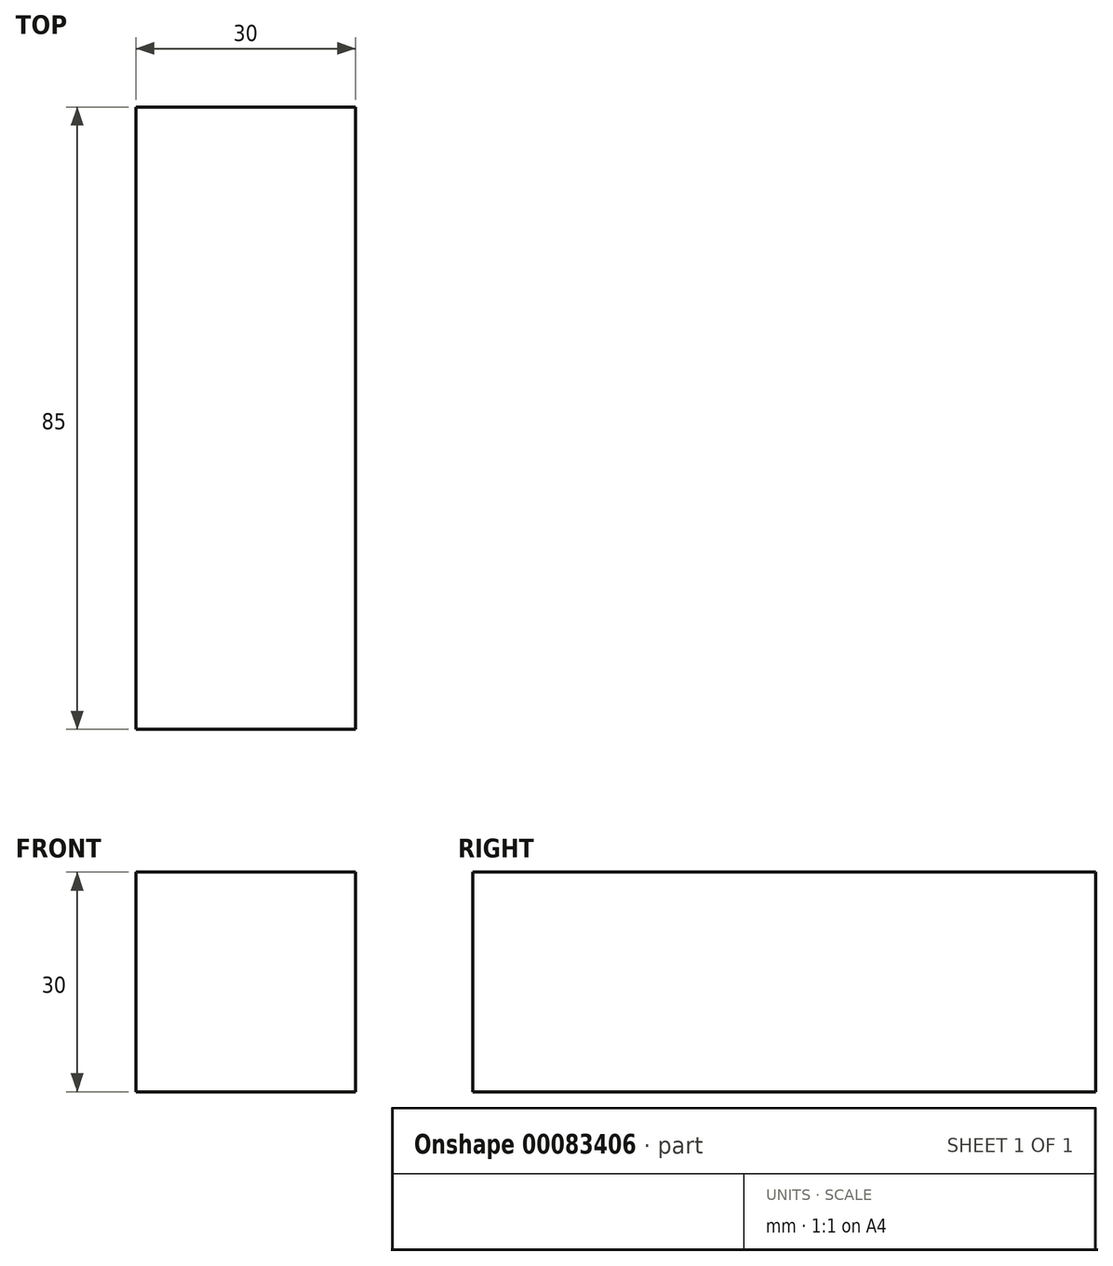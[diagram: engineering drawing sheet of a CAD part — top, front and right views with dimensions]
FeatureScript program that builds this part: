
annotation { "Feature Type Name" : "Feature", "Feature Type Description" : "" }
export const myFeature = defineFeature(function(context is Context, id is Id, definition is map)
    precondition{}
    {
        {
            var Q0;
            Q0=qCreatedBy(makeId("Right.planeOp"),FACE);
            var sketch = newSketch(context, id + "F0", { "sketchPlane" : qUnion([Q0])});
            skLineSegment(sketch, "E0.bottom", {"start": v(42.5, 15) * mm, "end": v(-42.5, 15) * mm});
            skLineSegment(sketch, "E0.top", {"start": v(42.5, -15) * mm, "end": v(-42.5, -15) * mm});
            skLineSegment(sketch, "E0.left", {"start": v(42.5, 15) * mm, "end": v(42.5, -15) * mm});
            skLineSegment(sketch, "E0.right", {"start": v(-42.5, 15) * mm, "end": v(-42.5, -15) * mm});
            skPoint(sketch, "E0.middle", {"position": v(0, 0) * mm});
            skLineSegment(sketch, "E1.bottom", {"start": v(88.8, 61.92) * mm, "end": v(68.8, 61.92) * mm});
            skLineSegment(sketch, "E1.top", {"start": v(88.8, 31.92) * mm, "end": v(68.8, 31.92) * mm});
            skLineSegment(sketch, "E1.left", {"start": v(88.8, 61.92) * mm, "end": v(88.8, 31.92) * mm});
            skLineSegment(sketch, "E1.right", {"start": v(68.8, 61.92) * mm, "end": v(68.8, 31.92) * mm});
            skPoint(sketch, "E1.middle", {"position": v(78.8, 46.92) * mm});
            skLineSegment(sketch, "E2", {"start": v(42.5, 15) * mm, "end": v(42.5, 32.3) * mm});
            skArc(sketch, "E3", {"start": v(42.5, 32.3) * mm, "mid": v(45.35, 39.16) * mm, "end": v(52.22, 42.01) * mm});
            skLineSegment(sketch, "E4", {"start": v(52.22, 42.01) * mm, "end": v(80.34, 42.01) * mm});
            skLineSegment(sketch, "E5.0", {"start": v(52.22, 57.01) * mm, "end": v(80.34, 57.01) * mm});
            skArc(sketch, "E5.1", {"start": v(27.5, 32.3) * mm, "mid": v(34.74, 49.77) * mm, "end": v(52.22, 57.01) * mm});
            skLineSegment(sketch, "E5.2", {"start": v(27.5, 15) * mm, "end": v(27.5, 32.3) * mm});
            skLineSegment(sketch, "E6", {"start": v(80.34, 31.92) * mm, "end": v(80.34, 34.97) * mm});
            skLineSegment(sketch, "E7", {"start": v(80.34, 34.97) * mm, "end": v(80.34, 61.92) * mm});
            skSolve(sketch);
        }
        {
            var Q0;
            Q0=makeQuery(id+"F0.imprint","IMPRINT",FACE,{"disambiguationData":[TD([[makeQuery(id+"F0.imprint","IMPRINT",EDGE,{"derivedFrom":sQuery(id+"F0.wireOp",EDGE,"E0.top")}),-1.0]])]});
            extrude(context, id + "F1", {"entities" : qUnion([Q0]), "endBound" : BoundingType.SYMMETRIC, "depth" : 30 * mm});
        }
    });
